# Revit family: Datchik polozheniya magnitogerkonovyy SK555
name_source: partatom
category: Датчики
units: mm (PartAtom-declared; Revit-internal decimal feet)

## family parameters
Всегда вертикально = Да
Заголовок OmniClass = Communication and Data Processing Equipment
На основе рабочей плоскости = Нет
Номер OmniClass = 23.85.50.17
Общий = Нет
При загрузке вырезать с полостями = Нет
Размер круглого соединителя = Использовать диаметр
Сохранять ориентацию аннотаций = Нет
Тип детали = Нормальный
Точка принадлежности помещению = Нет

## types (1)
- Датчик положения магнитогерконовый СК555 ABS
    ADSK_Единица измерения = шт.
    ADSK_Завод-изготовитель = ООО НПП «МАГНИТО-КОНТАКТ»
    ADSK_Масса = 0.02
    ADSK_Материал = ABS пластик
    ADSK_Наименование = Датчик положения магнитогерконовый СК555
    ADSK_Наименование краткое = СК555
    ADSK_Обозначение = АТФЕ.425119.119
    ADSK_Примечание = Датчик предназначен для открытой установки на поверхности охраняемой конструкции.
    ADSK_Размер_Высота = 10 мм
    ADSK_Размер_Длина = 20 мм
    ADSK_Размер_Ширина = 15 мм
    URL = https://m-kontakt.ru
    Изготовитель = ООО НПП «МАГНИТО-КОНТАКТ»
    Кабель = Кабельный вывод
    Максимальная мощность = 10 Вт
    Напряжение = от 0,02 до 72 В
    Описание = Датчик положения магнитогерконовый СК555 (далее датчик) предназначен для блокировки дверных и оконных проемов, других конструктивных элементов зданий и сооружений на открывание или смещение с выдачей извещения о тревоге на пульт централизованного наблюдения, прибор приёмно-контрольный или концентратор размыканием шлейфа сигнализации контактами встроенного геркона.
    Отметка по умолчанию = 0 мм
    Провод = Да
    Срок службы = не менее 8 лет
    Степень защиты оболочки = IP66
    Тип геркона = Нормально разомкнутый
